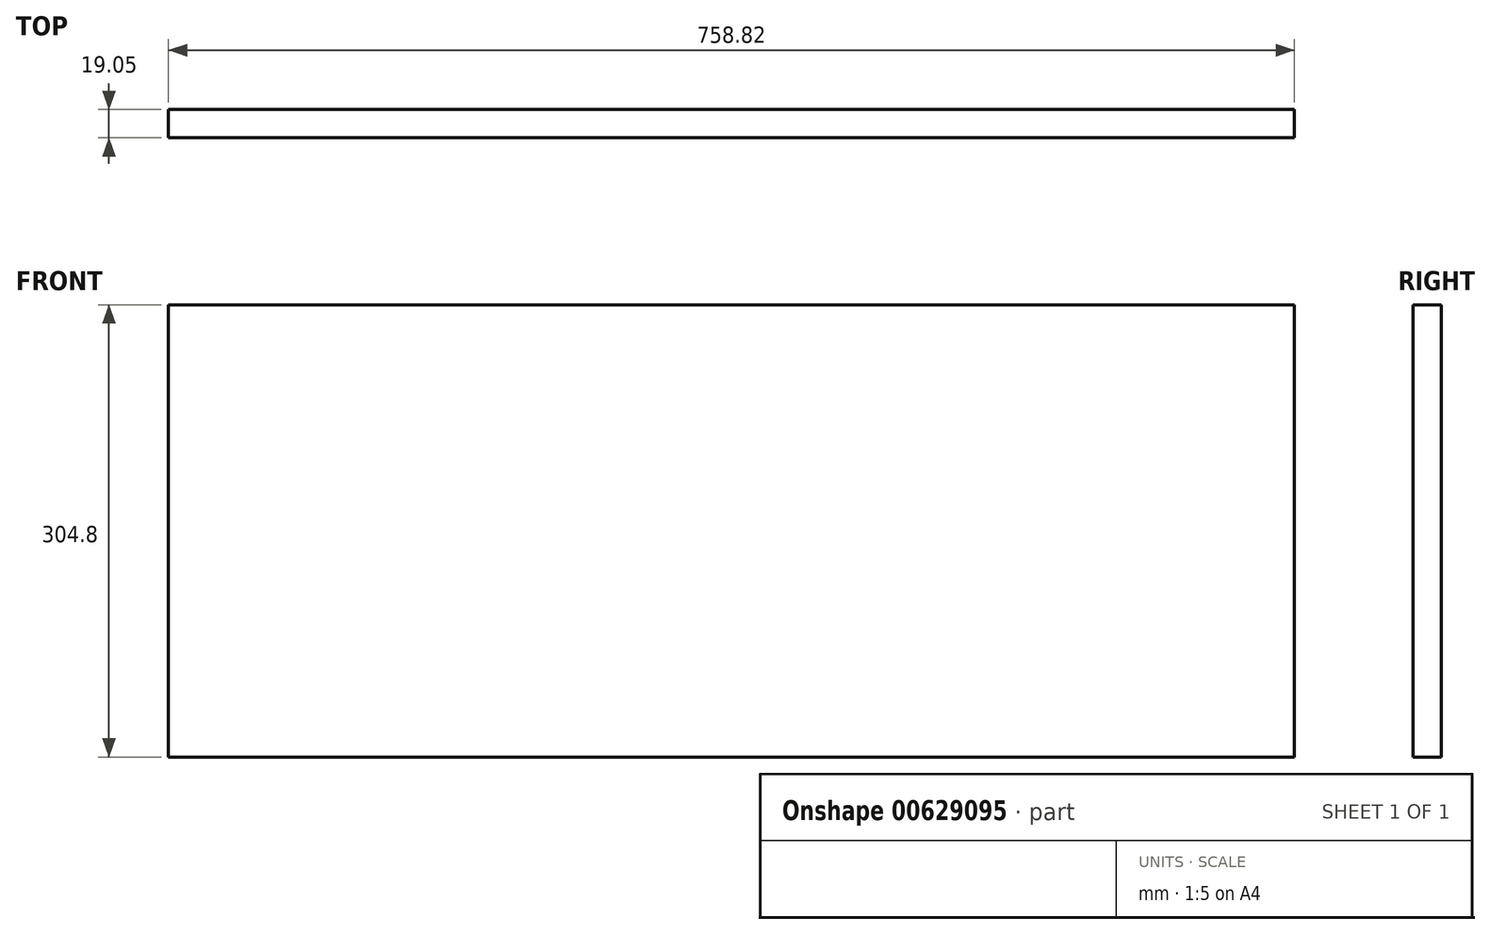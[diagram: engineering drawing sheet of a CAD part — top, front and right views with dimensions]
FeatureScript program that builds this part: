
annotation { "Feature Type Name" : "Feature", "Feature Type Description" : "" }
export const myFeature = defineFeature(function(context is Context, id is Id, definition is map)
    precondition{}
    {
        {
            var Q0;
            Q0=qCreatedBy(makeId("Front.planeOp"),FACE);
            var sketch = newSketch(context, id + "F0", { "sketchPlane" : qUnion([Q0])});
            skLineSegment(sketch, "E0.bottom", {"start": v(379.41, 152.4) * mm, "end": v(-379.41, 152.4) * mm});
            skLineSegment(sketch, "E0.top", {"start": v(379.41, -152.4) * mm, "end": v(-379.41, -152.4) * mm});
            skLineSegment(sketch, "E0.left", {"start": v(379.41, 152.4) * mm, "end": v(379.41, -152.4) * mm});
            skLineSegment(sketch, "E0.right", {"start": v(-379.41, 152.4) * mm, "end": v(-379.41, -152.4) * mm});
            skPoint(sketch, "E0.middle", {"position": v(0, 0) * mm});
            skSolve(sketch);
        }
        {
            var Q0;
            Q0=makeQuery(id+"F0.imprint","IMPRINT",FACE,{"disambiguationData":[TD([[makeQuery(id+"F0.imprint","IMPRINT",EDGE,{"derivedFrom":sQuery(id+"F0.wireOp",EDGE,"E0.bottom")}),1.0]])]});
            extrude(context, id + "F1", {"entities" : qUnion([Q0]), "depth" : 19.05 * mm, "offsetDistance" : 25.4 * mm});
        }
    });
